# Revit family: EBRE-LED-414x-MPOx
name_source: partatom
category: Leuchten
units: mm (PartAtom-declared; Revit-internal decimal feet)

## family parameters
Basisbauteil = Fläche
Beim Laden mit Abzugskörper schneiden = Nein
Bemaßung runder Anschluss = Durchmesser verwenden
Gemeinsam genutzt = Nein
Lichtquelle = Ja
OmniClass-Nummer = 23.80.70.11
OmniClass-Titel = Luminaries for Internal Lighting
Raumberechnungspunkt = Nein
Teiletyp = Normal

## types (8) — shared parameters
Baugruppenkennzeichen = D5020200
Datei für fotometrisches Netz = EBRE-LED 4146200-840 MPO.IES
Emissionsform beim Rendern sichtbar = Nein
Farbfilter = 16777215
Farbtemperaturverschiebung bei Dämpfen der Lampe = <Keine Auswahl>
Hersteller = RIDI Leuchten GmbH
Lampe = LED
Neigungswinkel = 90.00°
URL = www.ridi.de
Von Breite des Rechtecks ausssenden = 560 mm  [stored 1.83727 ft]
Von Länge des Rechtecks aussenden = 560 mm  [stored 1.83727 ft]
brand = RIDI
conformity mark = CE
electrical safety class = 1
height = 90 mm  [stored 0.295276 ft]
ingress protection (IP) code = IP20
length = 622 mm  [stored 2.04068 ft]
nominal frequency = 50-60Hz
nominal voltage = 230
voltage type (AC, DC, UC) = AC
weight = 6,7kg
width = 622 mm  [stored 2.04068 ft]
zero-valued in all types: Vorgabe-Ansicht

## per-type parameters (varying)
| type | Modell | Scheinlast | rated input power |
| EBRE-LED 414/2500-830 MPO | 0822903 | 16 VA | 16 |
| EBRE-LED 414/2500-830 MPO-DA | 0832903 | 16 VA | 16 |
| EBRE-LED 414/2700-840 MPO | 0822904 | 16 VA | 16 |
| EBRE-LED 414/2700-840 MPO-DA | 0832904 | 16 VA | 16 |
| EBRE-LED 414/6000-830 MPO | 0822905 | 39 VA | 39 |
| EBRE-LED 414/6000-830 MPO-DA | 0832905 | 39 VA | 39 |
| EBRE-LED 414/6200-840 MPO | 0822906 | 39 VA | 39 |
| EBRE-LED 414/6200-840 MPO-DA | 0832906 | 39 VA | 39 |

note: column(s) folded — value = type name in every type: product name

note: [stored X ft] marks values corroborated as IEEE doubles in the binary element streams (Revit-internal decimal feet)
